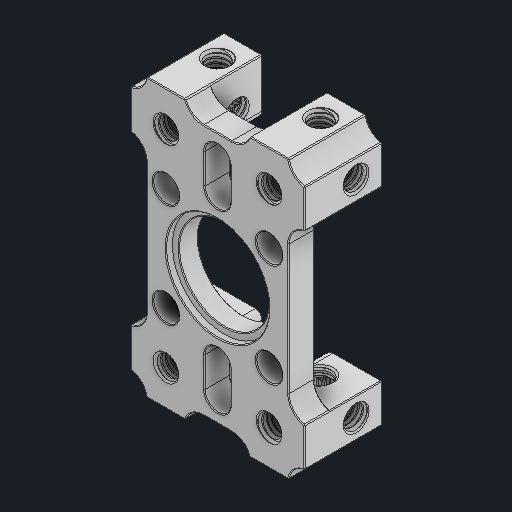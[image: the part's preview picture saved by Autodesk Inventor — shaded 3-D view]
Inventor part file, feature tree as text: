
AUTODESK INVENTOR PART (.ipt)
format: ipt  version: 2024 (Build 280153000, 153)  size: 9,178,112 bytes
history: native  units: in
note: dims shown in document units (in); Inventor stores cm internally (conversion verified against a paired STEP export)
features: chamfer x1
ambient origin geometry x8: Origin, YZ Plane, XZ Plane, XY Plane, X Axis, Y Axis, Z Axis, Center Point
bodies: Solid1 (feature_tree)
feature tree (1):
  chamfer  "Chamfer7"  [1 undecoded]
note: 1 required parameter value undecoded (feature->parameter linkage not recoverable at this tier; creation-order binding heuristic only, values carry confidence <= 0.55)
